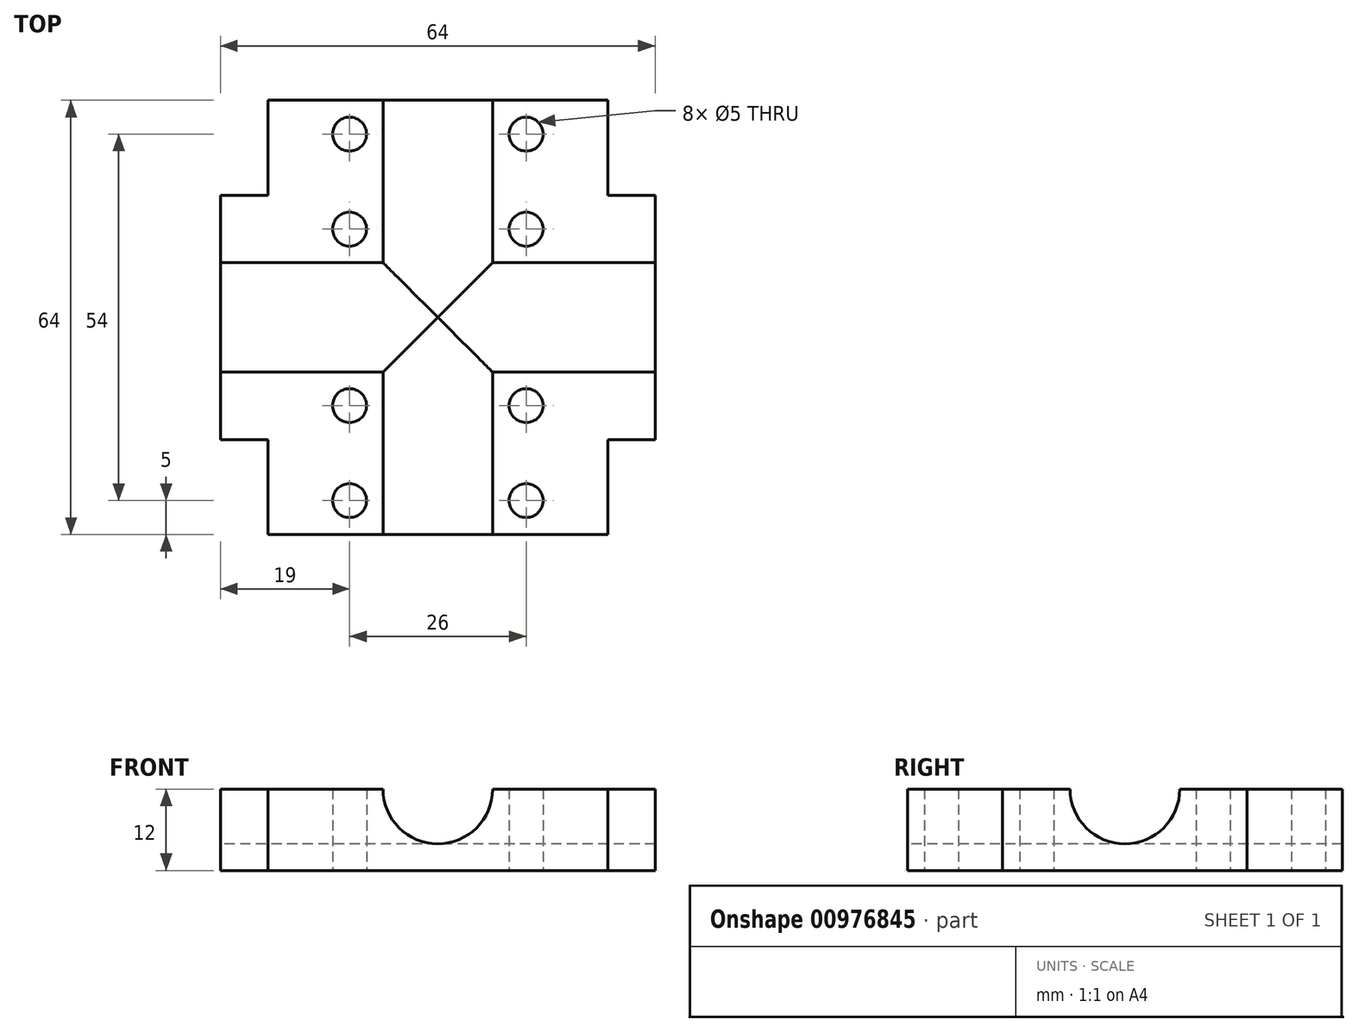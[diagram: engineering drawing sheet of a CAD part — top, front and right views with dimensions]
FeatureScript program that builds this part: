
annotation { "Feature Type Name" : "Feature", "Feature Type Description" : "" }
export const myFeature = defineFeature(function(context is Context, id is Id, definition is map)
    precondition{}
    {
        {
            var Q0;
            Q0=qCreatedBy(makeId("Top.planeOp"),FACE);
            var sketch = newSketch(context, id + "F0", { "sketchPlane" : qUnion([Q0])});
            skLineSegment(sketch, "E0.bottom", {"start": v(32, -32) * mm, "end": v(-32, -32) * mm});
            skLineSegment(sketch, "E0.top", {"start": v(32, 32) * mm, "end": v(-32, 32) * mm});
            skLineSegment(sketch, "E0.left", {"start": v(32, -32) * mm, "end": v(32, 32) * mm});
            skLineSegment(sketch, "E0.right", {"start": v(-32, -32) * mm, "end": v(-32, 32) * mm});
            skPoint(sketch, "E0.middle", {"position": v(0, 0) * mm});
            skLineSegment(sketch, "E1", {"start": v(-32, 32) * mm, "end": v(-32, -18) * mm, "construction": true});
            skLineSegment(sketch, "E2", {"start": v(-32, -18) * mm, "end": v(-25, -18) * mm, "construction": true});
            skLineSegment(sketch, "E3.bottom", {"start": v(-25, -18) * mm, "end": v(-32, -18) * mm});
            skLineSegment(sketch, "E3.top", {"start": v(-25, -32) * mm, "end": v(-32, -32) * mm});
            skLineSegment(sketch, "E3.left", {"start": v(-25, -18) * mm, "end": v(-25, -32) * mm});
            skLineSegment(sketch, "E3.right", {"start": v(-32, -18) * mm, "end": v(-32, -32) * mm});
            skLineSegment(sketch, "E4.MirrorCS", {"start": v(32, -18) * mm, "end": v(25, -18) * mm, "construction": true});
            skLineSegment(sketch, "E5.MirrorCS", {"start": v(25, -32) * mm, "end": v(32, -32) * mm});
            skLineSegment(sketch, "E6.bottom", {"start": v(25, -18) * mm, "end": v(32, -18) * mm});
            skLineSegment(sketch, "E6.left", {"start": v(25, -18) * mm, "end": v(25, -32) * mm});
            skLineSegment(sketch, "E6.right", {"start": v(32, -18) * mm, "end": v(32, -32) * mm});
            skLineSegment(sketch, "E7", {"start": v(0, -32) * mm, "end": v(13, -32) * mm, "construction": true});
            skLineSegment(sketch, "E8.MirrorCS", {"start": v(0, -32) * mm, "end": v(-13, -32) * mm, "construction": true});
            skLineSegment(sketch, "E9", {"start": v(32, 32) * mm, "end": v(32, 27) * mm, "construction": true});
            skLineSegment(sketch, "E10", {"start": v(32, 27) * mm, "end": v(-32, 27) * mm, "construction": true});
            skLineSegment(sketch, "E11", {"start": v(32, 27) * mm, "end": v(32, -13) * mm, "construction": true});
            skLineSegment(sketch, "E12", {"start": v(32, -13) * mm, "end": v(-32, -13) * mm, "construction": true});
            skLineSegment(sketch, "E13", {"start": v(13, -32) * mm, "end": v(13, -27) * mm, "construction": true});
            skLineSegment(sketch, "E14", {"start": v(13, -27) * mm, "end": v(-32, -27) * mm, "construction": true});
            skLineSegment(sketch, "E15", {"start": v(13, -27) * mm, "end": v(13, 30.1) * mm, "construction": true});
            skLineSegment(sketch, "E16", {"start": v(-13, -32) * mm, "end": v(-13, 31.2) * mm, "construction": true});
            skCircle(sketch, "E17", {"center": v(-13, -27) * mm, "radius": 2.5 * mm});
            skCircle(sketch, "E18", {"center": v(13, -27) * mm, "radius": 2.5 * mm});
            skCircle(sketch, "E19", {"center": v(13, -13) * mm, "radius": 2.5 * mm});
            skCircle(sketch, "E20", {"center": v(-13, -13) * mm, "radius": 2.5 * mm});
            skCircle(sketch, "E21", {"center": v(-13, 27) * mm, "radius": 2.5 * mm});
            skCircle(sketch, "E22", {"center": v(13, 27) * mm, "radius": 2.5 * mm});
            skLineSegment(sketch, "E23.bottom", {"start": v(-32, 32) * mm, "end": v(-25, 32) * mm});
            skLineSegment(sketch, "E23.top", {"start": v(-32, 18) * mm, "end": v(-25, 18) * mm});
            skLineSegment(sketch, "E23.left", {"start": v(-32, 32) * mm, "end": v(-32, 18) * mm});
            skLineSegment(sketch, "E23.right", {"start": v(-25, 32) * mm, "end": v(-25, 18) * mm});
            skLineSegment(sketch, "E24.bottom", {"start": v(32, 32) * mm, "end": v(25, 32) * mm});
            skLineSegment(sketch, "E24.top", {"start": v(32, 18) * mm, "end": v(25, 18) * mm});
            skLineSegment(sketch, "E24.left", {"start": v(32, 32) * mm, "end": v(32, 18) * mm});
            skLineSegment(sketch, "E24.right", {"start": v(25, 32) * mm, "end": v(25, 18) * mm});
            skCircle(sketch, "E25.MirrorC", {"center": v(-13, 13) * mm, "radius": 2.5 * mm});
            skCircle(sketch, "E26.MirrorC", {"center": v(13, 13) * mm, "radius": 2.5 * mm});
            skSolve(sketch);
        }
        {
            var Q0;
            {var subQ2=sQuery(id+"F0.wireOp",EDGE,"E3.bottom");Q0=makeQuery(id+"F0.imprint","IMPRINT",FACE,{"disambiguationData":[TD([[makeQuery(id+"F0.imprint","IMPRINT",EDGE,{"derivedFrom":subQ2}),-1.0]])]});}
            var Q1;
            {var subQ2=sQuery(id+"F0.wireOp",EDGE,"E3.bottom");Q1=makeQuery(id+"F0.imprint","IMPRINT",FACE,{"disambiguationData":[TD([[makeQuery(id+"F0.imprint","IMPRINT",EDGE,{"derivedFrom":subQ2}),-1.0]])]});}
            extrude(context, id + "F1", {"entities" : qUnion([Q0, Q1]), "depth" : 12 * mm, "offsetDistance" : 25 * mm});
        }
        {
            var Q0;
            {var subQ4=sQuery(id+"F0.wireOp",EDGE,"E6.bottom");Q0=makeQuery(id+"F0.imprint","IMPRINT",FACE,{"disambiguationData":[TD([[makeQuery(id+"F0.imprint","IMPRINT",EDGE,{"derivedFrom":subQ4}),-1.0]])]});}
            var Q1;
            {var subQ4=sQuery(id+"F0.wireOp",EDGE,"E3.bottom");Q1=makeQuery(id+"F0.imprint","IMPRINT",FACE,{"disambiguationData":[TD([[makeQuery(id+"F0.imprint","IMPRINT",EDGE,{"derivedFrom":subQ4}),1.0]])]});}
            extrude(context, id + "F2", {"entities" : qUnion([Q0, Q1]), "operationType" : NewBodyOperationType.REMOVE, "endBound" : BoundingType.THROUGH_ALL, "depth" : 25 * mm, "offsetDistance" : 25 * mm});
        }
        {
            var Q0;
            Q0=makeQuery(id+"F1.opExtrude","SWEPT_FACE",FACE,{"disambiguationData":[OSD([sQuery(id+"F0.wireOp",EDGE,"E0.bottom")])]});
            var sketch = newSketch(context, id + "F3", { "sketchPlane" : qUnion([Q0])});
            skCircle(sketch, "E27", {"center": v(0, 12) * mm, "radius": 8.07 * mm});
            skSolve(sketch);
        }
        {
            var Q0;
            Q0=qSketchRegion(id+"F3",true);
            extrude(context, id + "F4", {"entities" : qUnion([Q0]), "operationType" : NewBodyOperationType.REMOVE, "endBound" : BoundingType.THROUGH_ALL, "oppositeDirection" : true, "depth" : 25 * mm, "offsetDistance" : 25 * mm});
        }
        {
            var Q0;
            Q0=makeQuery(id+"F1.opExtrude","SWEPT_FACE",FACE,{"disambiguationData":[OSD([sQuery(id+"F0.wireOp",EDGE,"E0.right")])]});
            var sketch = newSketch(context, id + "F5", { "sketchPlane" : qUnion([Q0])});
            skCircle(sketch, "E28", {"center": v(0, 12) * mm, "radius": 8.07 * mm});
            skSolve(sketch);
        }
        {
            var Q0;
            {var subQ0=sQuery(id+"F5.wireOp",EDGE,"E28");var subQ1=makeQuery(id+"F1.opExtrude","CAP_EDGE",EDGE,{"disambiguationData":[OSD([sQuery(id+"F0.wireOp",EDGE,"E0.right")])],"isStart":false});var subQ2=makeQuery(id+"F5.imprint","INTERSECT",VERTEX,{"disambiguationData":[OD(0.0)],"derivedFrom":[subQ1,subQ0]});Q0=makeQuery(id+"F5.imprint","IMPRINT",FACE,{"disambiguationData":[TD([[makeQuery(id+"F5.imprint","IMPRINT",EDGE,{"disambiguationData":[TD([[subQ2,1.0]])],"derivedFrom":subQ0}),1.0]])]});}
            extrude(context, id + "F6", {"entities" : qUnion([Q0]), "operationType" : NewBodyOperationType.REMOVE, "endBound" : BoundingType.THROUGH_ALL, "oppositeDirection" : true, "depth" : 25 * mm, "offsetDistance" : 25 * mm});
        }
    });
